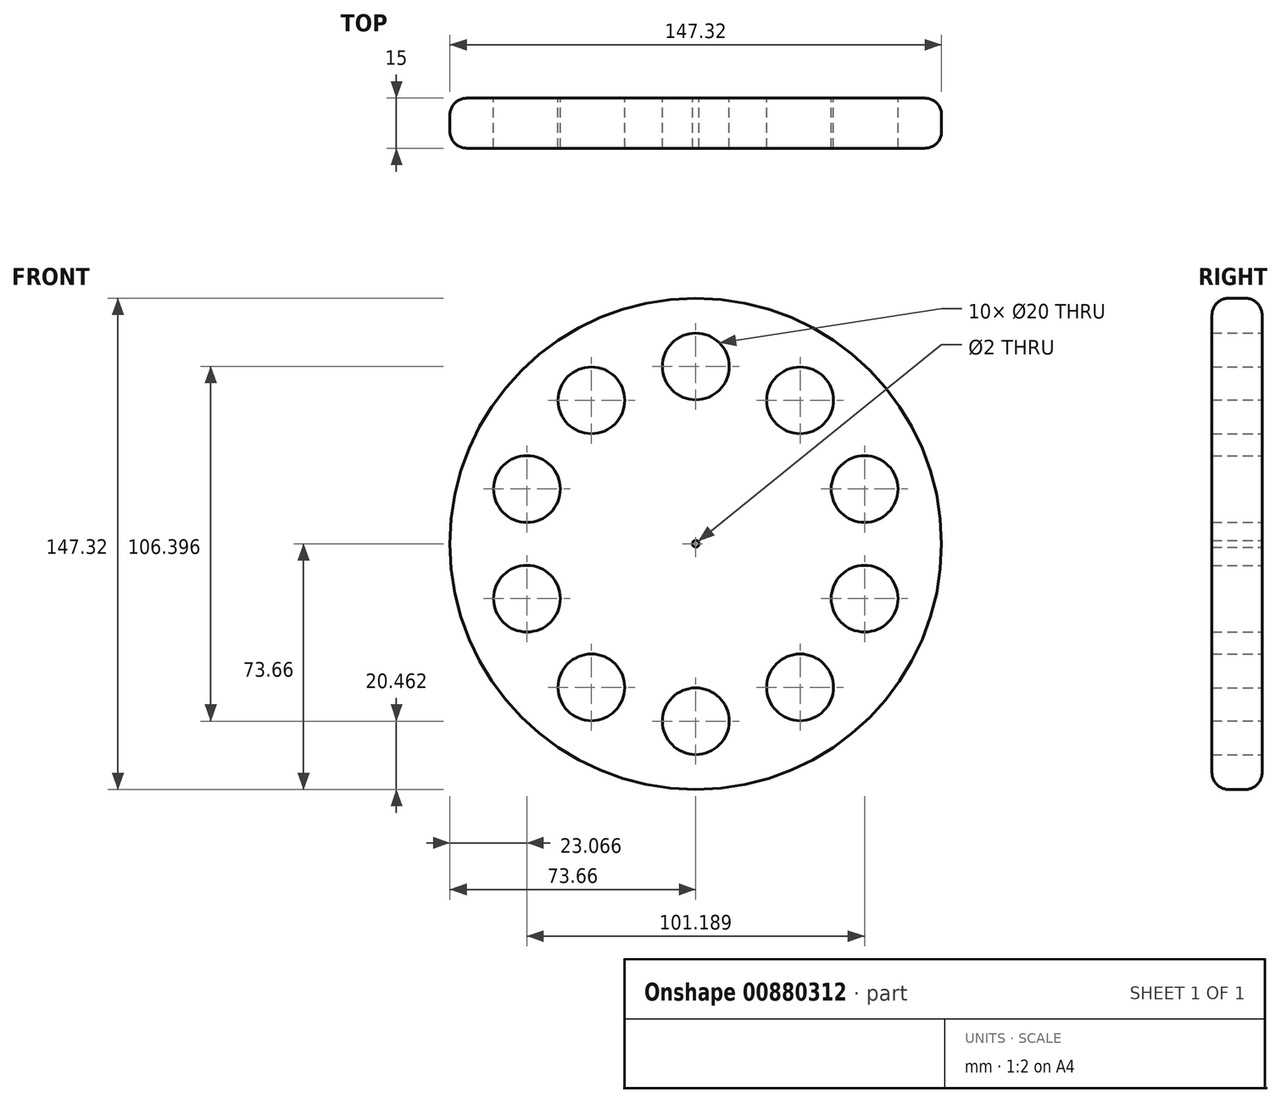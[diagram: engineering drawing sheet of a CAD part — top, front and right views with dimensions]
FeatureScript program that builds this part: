
annotation { "Feature Type Name" : "Feature", "Feature Type Description" : "" }
export const myFeature = defineFeature(function(context is Context, id is Id, definition is map)
    precondition{}
    {
        {
            var Q0;
            Q0=qCreatedBy(makeId("Front.planeOp"),FACE);
            var sketch = newSketch(context, id + "F0", { "sketchPlane" : qUnion([Q0])});
            skCircle(sketch, "E0", {"center": v(0, 0) * mm, "radius": 73.66 * mm});
            skCircle(sketch, "E1", {"center": v(0, 53.2) * mm, "radius": 10 * mm});
            skCircle(sketch, "E2.1.0", {"center": v(-31.27, 43.04) * mm, "radius": 10 * mm});
            skCircle(sketch, "E2.2.0", {"center": v(-50.6, 16.44) * mm, "radius": 10 * mm});
            skCircle(sketch, "E2.3.0", {"center": v(-50.6, -16.44) * mm, "radius": 10 * mm});
            skCircle(sketch, "E2.4.0", {"center": v(-31.27, -43.04) * mm, "radius": 10 * mm});
            skCircle(sketch, "E2.5.0", {"center": v(0, -53.2) * mm, "radius": 10 * mm});
            skCircle(sketch, "E2.6.0", {"center": v(31.27, -43.04) * mm, "radius": 10 * mm});
            skCircle(sketch, "E2.7.0", {"center": v(50.6, -16.44) * mm, "radius": 10 * mm});
            skCircle(sketch, "E2.8.0", {"center": v(50.6, 16.44) * mm, "radius": 10 * mm});
            skCircle(sketch, "E2.9.0", {"center": v(31.27, 43.04) * mm, "radius": 10 * mm});
            skSolve(sketch);
        }
        {
            var Q0;
            Q0 = qSketchRegion(id + "F0", true);
            extrude(context, id + "F1", {"entities" : qUnion([Q0]), "depth" : 15 * mm, "offsetDistance" : 25 * mm});
        }
        {
            var Q0;
            Q0=qCreatedBy(makeId("Front.planeOp"),FACE);
            var sketch = newSketch(context, id + "F2", { "sketchPlane" : qUnion([Q0])});
            skCircle(sketch, "E3", {"center": v(0, 0) * mm, "radius": 1 * mm});
            skSolve(sketch);
        }
        {
            var Q0;
            Q0 = qSketchRegion(id + "F2", true);
            extrude(context, id + "F3", {"entities" : qUnion([Q0]), "operationType" : NewBodyOperationType.REMOVE, "depth" : 25 * mm, "offsetDistance" : 25 * mm});
        }
        {
            var Q0;
            Q0=makeQuery(id+"F1.opExtrude","CAP_EDGE",EDGE,{"disambiguationData":[OSD([sQuery(id+"F0.wireOp",EDGE,"E0")])],"isStart":false});
            var Q1;
            Q1=makeQuery(id+"F1.opExtrude","CAP_EDGE",EDGE,{"disambiguationData":[OSD([sQuery(id+"F0.wireOp",EDGE,"E0")])],"isStart":true});
            fillet(context, id + "F4", {"entities" : qUnion([Q0, Q1]), "radius" : 5 * mm, "tangentPropagation" : true, "allowEdgeOverflow" : false});
        }
    });
